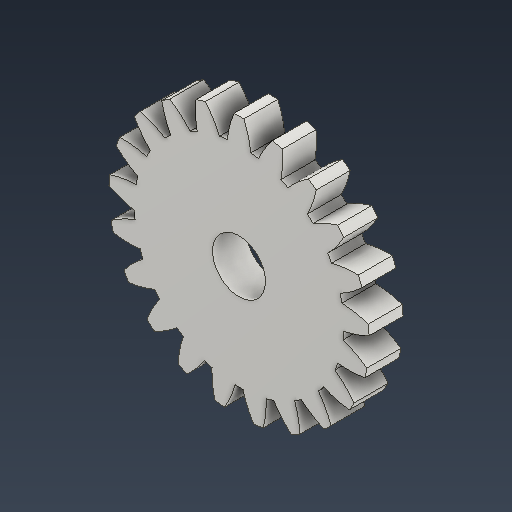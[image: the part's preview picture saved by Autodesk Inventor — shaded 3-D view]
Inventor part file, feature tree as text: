
AUTODESK INVENTOR PART (.ipt)
format: ipt  version: 2025.3 (Build 293356000, 356)  size: 247,808 bytes
history: native  units: mm (DEFAULTED — no unit token found)
features: plane x3, other x3, extrude x2, sketch x2
ambient origin geometry x8: Origin, YZ Plane, XZ Plane, XY Plane, X Axis, Y Axis, Z Axis, Center Point
bodies: Solid1 (feature_tree)
feature tree (10):
  extrude  "Extrusion1"  Depth=3.0mm TaperAngle=0.0deg
  plane  "Work Plane2"
  plane  "Work Plane8"
  plane  "Work Plane9"
  other  "正齒輪"
  extrude  "擠出2"  Depth=10.0mm
  sketch  "Sketch1"  dims[d0=23.0mm d1=3.0mm d2=0.0mm d3=21.0mm d4=10.0mm d5=0.0mm d16=17.5mm d17=0.0mm d34=1.495997mm d39=0.0mm d41=0.0mm d43=17.5mm d46=17.5mm d47=0.0mm d48=0.0mm d49=4.68mm d50=10.0mm d51=0.0mm]
  other  "Srf1"
  sketch  "草圖3"
  other  "節圓直徑"
